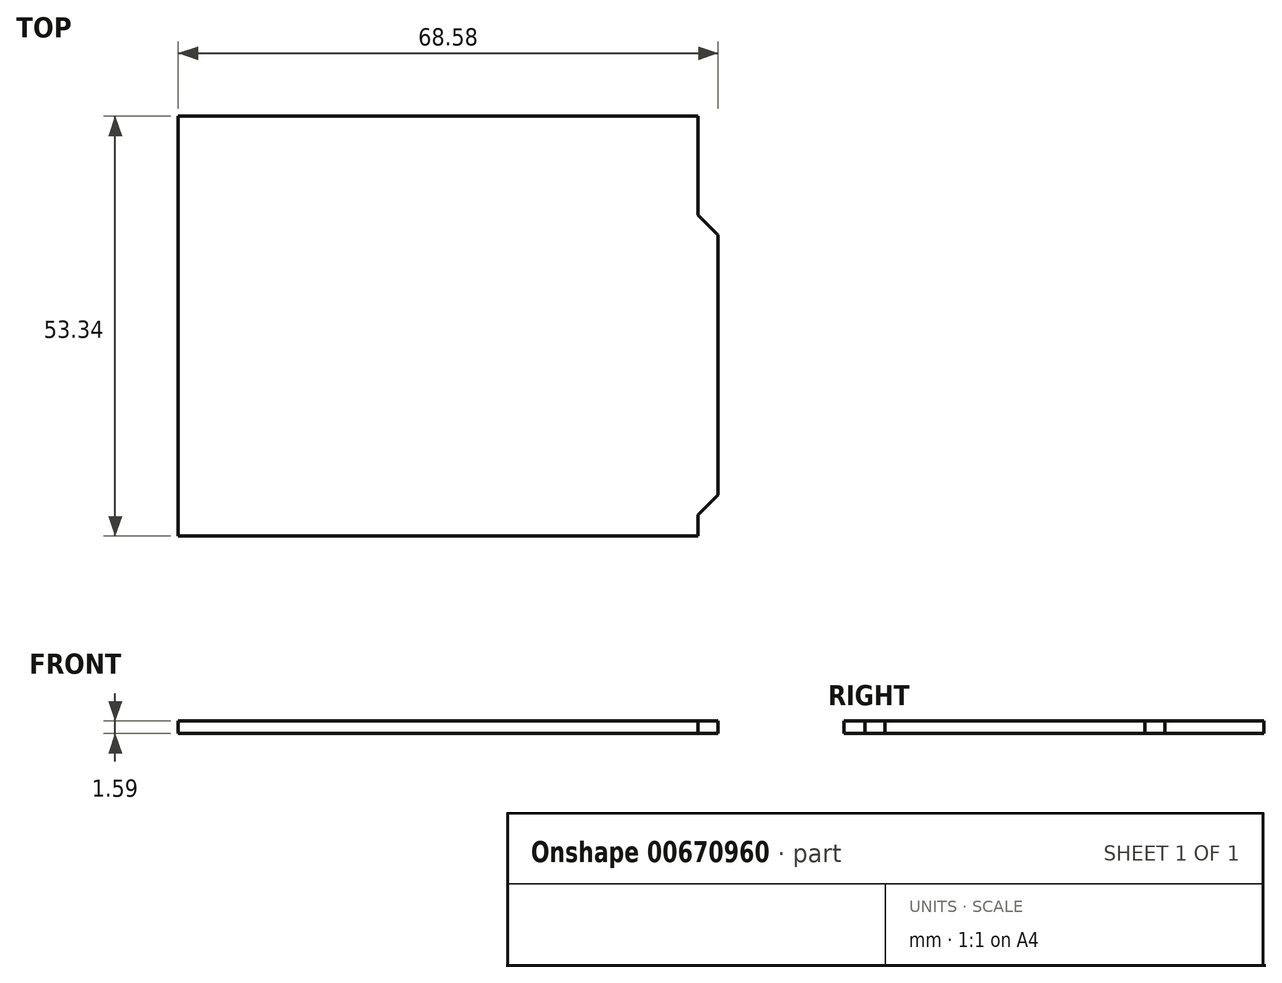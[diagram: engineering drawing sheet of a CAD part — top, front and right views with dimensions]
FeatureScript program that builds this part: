
annotation { "Feature Type Name" : "Feature", "Feature Type Description" : "" }
export const myFeature = defineFeature(function(context is Context, id is Id, definition is map)
    precondition{}
    {
        {
            var Q0;
            Q0=qCreatedBy(makeId("Top.planeOp"),FACE);
            var sketch = newSketch(context, id + "F0", { "sketchPlane" : qUnion([Q0])});
            skLineSegment(sketch, "E0.bottom", {"start": v(0, 0) * mm, "end": v(-66.04, 0) * mm});
            skLineSegment(sketch, "E0.top", {"start": v(0, 53.34) * mm, "end": v(-66.04, 53.34) * mm});
            skLineSegment(sketch, "E0.left", {"start": v(0, 0) * mm, "end": v(0, 53.34) * mm});
            skLineSegment(sketch, "E0.right", {"start": v(-66.04, 0) * mm, "end": v(-66.04, 53.34) * mm});
            skLineSegment(sketch, "E1", {"start": v(0, 40.77) * mm, "end": v(2.54, 38.23) * mm});
            skLineSegment(sketch, "E2", {"start": v(2.54, 38.23) * mm, "end": v(2.54, 5.2) * mm});
            skLineSegment(sketch, "E3", {"start": v(2.54, 5.2) * mm, "end": v(0, 2.67) * mm});
            skSolve(sketch);
        }
        {
            var Q0;
            Q0 = qSketchRegion(id + "F0", true);
            extrude(context, id + "F1", {"entities" : qUnion([Q0]), "depth" : 1.59 * mm, "offsetDistance" : 25 * mm});
        }
    });
